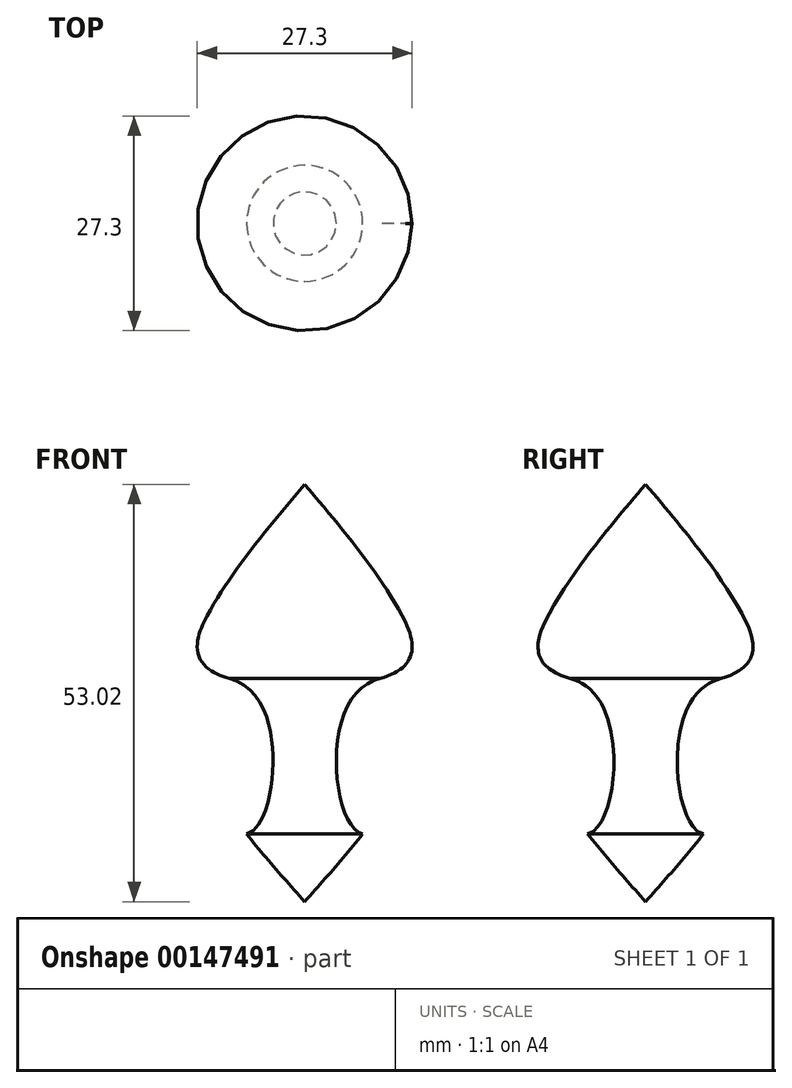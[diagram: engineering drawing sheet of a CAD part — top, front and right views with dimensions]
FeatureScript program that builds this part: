
annotation { "Feature Type Name" : "Feature", "Feature Type Description" : "" }
export const myFeature = defineFeature(function(context is Context, id is Id, definition is map)
    precondition{}
    {
        {
            var Q0;
            Q0=qCreatedBy(makeId("Front.planeOp"),FACE);
            var sketch = newSketch(context, id + "F0", { "sketchPlane" : qUnion([Q0])});
            skLineSegment(sketch, "E0", {"start": v(0, 53.02) * mm, "end": v(0, 0) * mm});
            skFitSpline(sketch, "E1", {"points": [v(0, 53.02) * mm, v(-15.34, 25.83) * mm, v(0, 0) * mm], "startDerivative": vector(-45.88, -54.29) * mm, "endDerivative": vector(46.18, -51.74) * mm});
            skFitSpline(sketch, "E2", {"points": [v(-7.62, 8.54) * mm, v(-15.34, 25.83) * mm, v(-6.02, 25.83) * mm, v(-7.62, 8.54) * mm]});
            skSolve(sketch);
        }
        {
            var Q0;
            {var subQ0=sQuery(id+"F0.wireOp",EDGE,"E0");Q0=makeQuery(id+"F0.imprint","IMPRINT",FACE,{"disambiguationData":[TD([[makeQuery(id+"F0.imprint","IMPRINT",EDGE,{"derivedFrom":subQ0}),-1.0]])]});}
            var Q1;
            {var subQ0=sQuery(id+"F0.wireOp",EDGE,"E0");Q1=makeQuery(id+"F0.imprint","IMPRINT",FACE,{"disambiguationData":[TD([[makeQuery(id+"F0.imprint","IMPRINT",EDGE,{"derivedFrom":subQ0}),-1.0]])]});}
            var Q2;
            Q2=sQuery(id+"F0.wireOp",EDGE,"E0");
            revolve(context, id + "F1", {"entities" : qUnion([Q0, Q1]), "axis" : qUnion([Q2]), "revolveType" : RevolveType.FULL});
        }
        {
            var Q0;
            {var subQ0=sQuery(id+"F0.wireOp",EDGE,"E2");var subQ1=sQuery(id+"F0.wireOp",EDGE,"E1");Q0=makeQuery(id+"F1.opRevolve","SWEPT_EDGE",EDGE,{"disambiguationData":[OSD([subQ1,subQ0]),TDD([makeQuery(id+"F0.imprint","INTERSECT",VERTEX,{"disambiguationData":[OD(0.0)],"derivedFrom":[subQ1,subQ0]})])]});}
            fillet(context, id + "F2", {"entities" : qUnion([Q0]), "radius" : 5.08 * mm, "tangentPropagation" : true, "rho" : 0.5, "crossSection" : FilletCrossSection.CONIC, "allowEdgeOverflow" : false});
        }
    });
